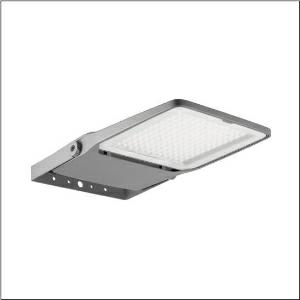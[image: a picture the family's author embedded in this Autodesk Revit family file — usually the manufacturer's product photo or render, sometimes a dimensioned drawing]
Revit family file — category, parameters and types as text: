
# Revit family: floodlight_fl_20_midi___pl52_5xa7682d3d2ac_85b5
name_source: partatom
category: Lighting Fixtures
units: mm (PartAtom-declared; Revit-internal decimal feet)

## family parameters
Cut with Voids When Loaded = No
Host = Face
Light Source = No
Part Type = Normal
Room Calculation Point = No
Round Connector Dimension = Use Diameter
Shared = No

## types (1)
- --- (1 x LED 5000K / CRI = 70 (unbekannt), 18250 lm, 5000K)
    Apparent Load = 142 VA
    CIE Flux Codes = 27 59 98 100 100
    Color Rendering = 70
    Color Temperature = 5000K
    Default Elevation = 1800 mm
    Description = Floodlight FL 20 midi, floodlight, primary light control with lens, of plastic, primary optical cover: protective disc, of toughened safety glass, transparent, light distribution: PL52, light emission: direct distribution, primary light characteristic: asymmetric, installation type: surface-mounted, LED High Power LED, rated luminous flux: 18.250 lm, light colour: 750, colour temperature: 5000K, control gear: ECG Plus, control: flexible luminous flux parameterisation, time-dependent luminous flux control, digital communication interface, power reduction, overheat protection, electronic power reduction, with terminal, 5-pole, max. 2.5mm², mains connection: 220..240V, AC, 50/60Hz, rated input power: 142W, LED unit, of diecast aluminium, powder-coated, Siteco® metallic grey (DB 702S), length: 731 mm, width: 450 mm, height: 76mm, housing frame, of diecast aluminium, powder-coated, Siteco® metallic grey (DB 702S), wall fastening, of steel, powder-coated, Siteco® metallic grey (DB 702S), DALIprotection rating (complete): IP66, insulation class (complete): insulation class II (safety insulation), certification: CE, ENEC, VDE, protection symbol: D, permissible ambient temperature for indoor applications: -40..+40°C, permissible ambient temperature for outdoor applications: -40..+50°C, standard: DIN EN 12944, packaging unit: 1 piece

Light Distribution: PL52
    Height = 76 mm
    Lamp = 1 x LED 5000K / CRI >= 70 (unbekannt)
    Lamp Light Flux = 18250 lm
    Lamp count = 1
    Length = 731 mm
    Luminous efficacy = 129 lm/W
    Manufacturer = Siteco
    ModVariant = No
    Model = 5XA7682D3D2AC
    Number of Poles = 1
    OnlyDefault = Yes
    Power Factor = 1
    Product Name = Floodlight FL 20 midi | PL52
    Product group = floodlight | pylon top
    ProductGroupID = 6101
    Protection Class = Protection class II
    Protection Degree = IP 66
    RLX_Detail_Level = 1
    RlxData = <blob elided: 92217 chars, md5=43fc93ed>
    Socket = socket
    Standby Power = 0 W
    System Light Flux = 18250 lm
    System Power = 142 W
    Type Comments = factory setting: luminous flux: 100 % | dim-lin: 254 | 489 mA
    Type Image = l_1005944.jpg
    URL = http://relux.com
    VarID = @adj_143151
    Voltage = 0 V
    Weight = 0.00 kg
    Width = 450 mm

## geometry (parser evidence)
native form markers: Blend x4, Sweep x13
no freeform markers — native parametric forms only
